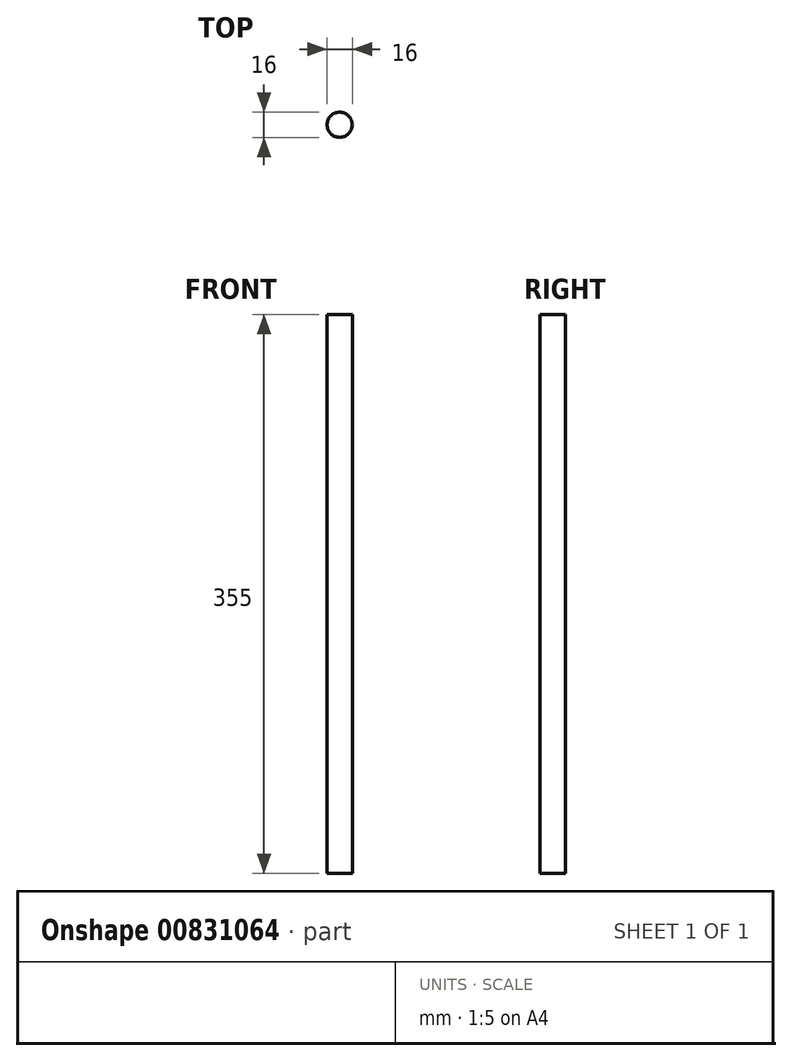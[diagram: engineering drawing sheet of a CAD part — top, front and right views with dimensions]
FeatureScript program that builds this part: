
annotation { "Feature Type Name" : "Feature", "Feature Type Description" : "" }
export const myFeature = defineFeature(function(context is Context, id is Id, definition is map)
    precondition{}
    {
        {
            var Q0;
            Q0=qCreatedBy(makeId("Top.planeOp"),FACE);
            var sketch = newSketch(context, id + "F0", { "sketchPlane" : qUnion([Q0])});
            skCircle(sketch, "E0", {"center": v(0, 0) * mm, "radius": 8 * mm});
            skSolve(sketch);
        }
        {
            var Q0;
            Q0=makeQuery(id+"F0.imprint","IMPRINT",FACE,{"disambiguationData":[TD([[makeQuery(id+"F0.imprint","IMPRINT",EDGE,{"derivedFrom":sQuery(id+"F0.wireOp",EDGE,"E0")}),1.0]])]});
            extrude(context, id + "F1", {"entities" : qUnion([Q0]), "depth" : 355 * mm, "offsetDistance" : 25 * mm});
        }
    });
